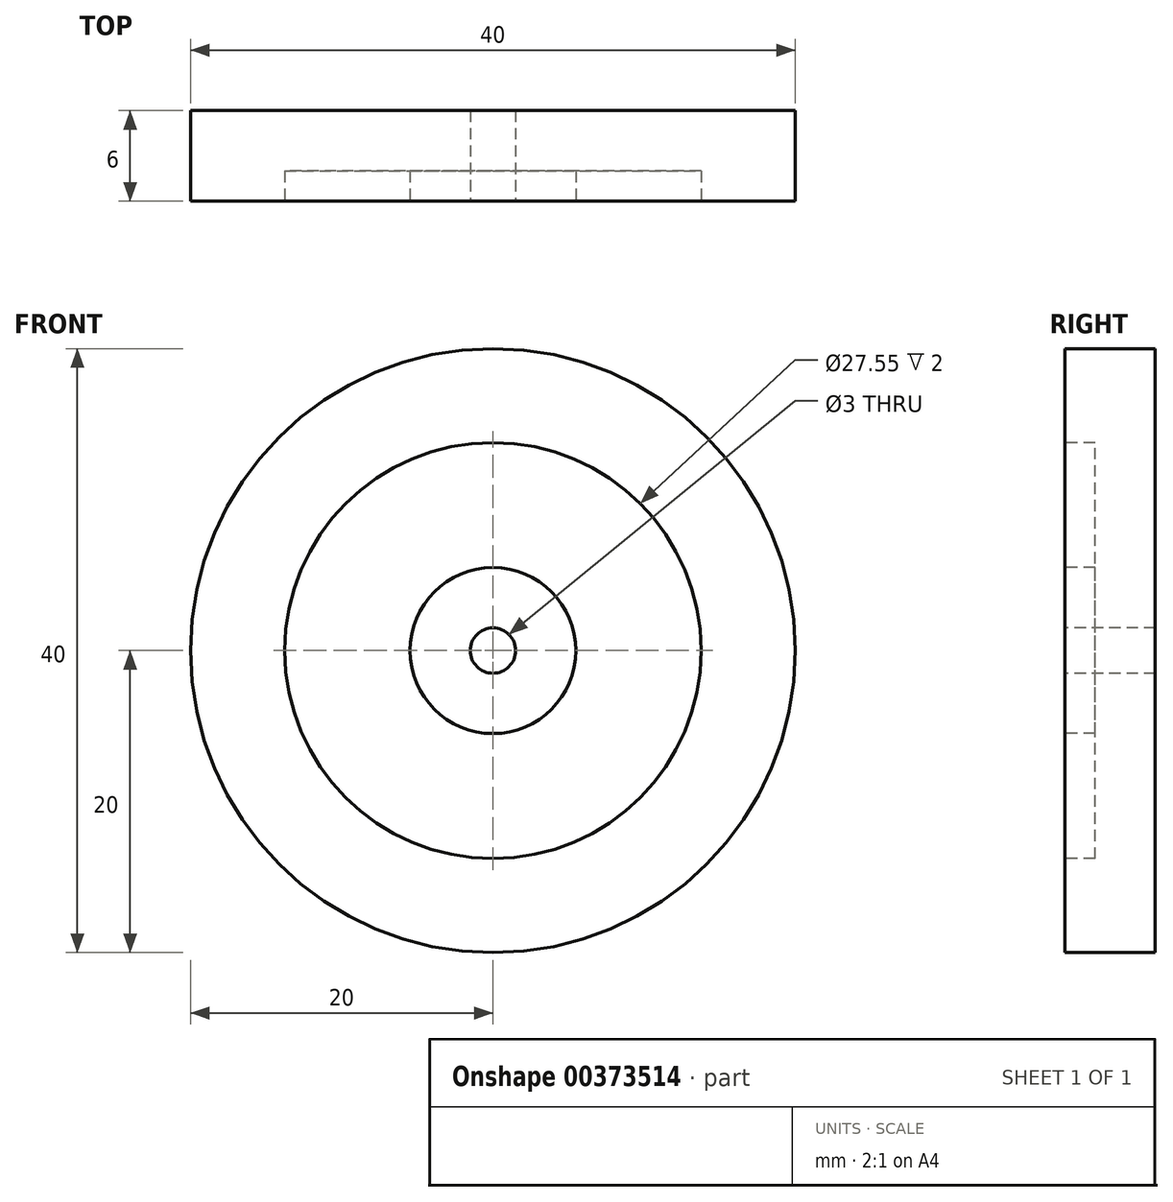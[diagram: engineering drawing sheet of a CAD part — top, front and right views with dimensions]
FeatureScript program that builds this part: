
annotation { "Feature Type Name" : "Feature", "Feature Type Description" : "" }
export const myFeature = defineFeature(function(context is Context, id is Id, definition is map)
    precondition{}
    {
        {
            var Q0;
            Q0=qCreatedBy(makeId("Front.planeOp"),FACE);
            var sketch = newSketch(context, id + "F0", { "sketchPlane" : qUnion([Q0])});
            skCircle(sketch, "E0", {"center": v(0, 0) * mm, "radius": 20 * mm});
            skSolve(sketch);
        }
        {
            var Q0;
            Q0=makeQuery(id+"F0.imprint","IMPRINT",FACE,{"disambiguationData":[TD([[makeQuery(id+"F0.imprint","IMPRINT",EDGE,{"derivedFrom":sQuery(id+"F0.wireOp",EDGE,"E0")}),1.0]])]});
            extrude(context, id + "F1", {"entities" : qUnion([Q0]), "depth" : 6 * mm});
        }
        {
            var Q0;
            Q0=makeQuery(id+"F1.opExtrude","CAP_FACE",FACE,{"disambiguationData":[OSD([sQuery(id+"F0.wireOp",EDGE,"E0")])],"isStart":false});
            var sketch = newSketch(context, id + "F2", { "sketchPlane" : qUnion([Q0])});
            skCircle(sketch, "E1", {"center": v(0, 0) * mm, "radius": 5.5 * mm});
            skCircle(sketch, "E2", {"center": v(0, 0) * mm, "radius": 13.77 * mm});
            skSolve(sketch);
        }
        {
            var Q0;
            Q0=makeQuery(id+"F2.imprint","IMPRINT",FACE,{"disambiguationData":[TD([[makeQuery(id+"F2.imprint","IMPRINT",EDGE,{"derivedFrom":sQuery(id+"F2.wireOp",EDGE,"E1")}),-1.0]])]});
            extrude(context, id + "F3", {"entities" : qUnion([Q0]), "operationType" : NewBodyOperationType.REMOVE, "oppositeDirection" : true, "depth" : 2 * mm});
        }
        {
            var Q0;
            Q0=sQuery(id+"F2.wireOp",VERTEX,"E2.center");
            var Q1;
            Q1=makeQuery(id+"F1.opExtrude","SWEPT_BODY",BODY,{"disambiguationData":[OSD([sQuery(id+"F0.wireOp",EDGE,"E0")])]});
            hole(context, id + "F4", {"style" : HoleStyle.SIMPLE, "endStyle" : HoleEndStyle.THROUGH, "holeDiameter" : 3 * mm, "isTappedThrough" : true, "tappedDepth" : 12 * mm, "tapClearance" : 3, "locations" : qUnion([Q0]), "scope" : qUnion([Q1])});
        }
    });
